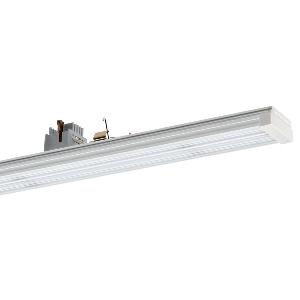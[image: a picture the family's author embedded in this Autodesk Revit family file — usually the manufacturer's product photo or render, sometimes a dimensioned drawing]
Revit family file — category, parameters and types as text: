
# Revit family: conveo_-_cvg_15000_840_xn-p_ea_5_226848239-00804961_3938
name_source: partatom
category: Lighting Fixtures
units: mm (PartAtom-declared; Revit-internal decimal feet)

## family parameters
Cut with Voids When Loaded = No
Host = Face
Light Source = No
Part Type = Normal
Room Calculation Point = No
Round Connector Dimension = Use Diameter
Shared = No

## types (1)
- CONVEO - CVG 15000/840/xN-P/EA/5 (1 x LED, 13800 lm, 4000K)
    Apparent Load = 100 VA
    Approval mark = CE
    CIE Flux Codes = 57 84 97 100 100
    Color Rendering = 80-89
    Color Temperature = 4000K
    Control Gear = Electronic ballast
    Default Elevation = 1800 mm
    Description = CVG 15000/840/xN-P/EA/5|Continuous-row system|light source: LED|work equipment: Electronic ballast|connected load: 220-240 V, 50-60 Hz|Power consumption: approx. 100 W|luminous flux: 13800 lm|luminous efficacy: 138 lm/W|colour temperature: Cold white, ca. 4000 K|color rendering index (CRI): >= 80|chromaticity tolerance:  3 SDCM|System of protection: IP 54|class of protection: I|technology: Switchable|luminaire body|material: Aluminium|surface: Powder coatet|colour: White|lamp cover: Acrylic (PMMA), Satine|weight (net): approx. 2.2 kg|Fastening: Available separately|minimum ambient temperature: -25 ░C|maximum ambient temperature: 37 ░C|glare control: Prism optics (linear)|Approval mark: VDE - ENEC|
    Frequency = 50 Hz
    Height = 70 mm
    Lamp = 1 x LED
    Lamp Light Flux = 13800 lm
    Lamp count = 1
    Length = 1500 mm
    Luminous efficacy = 138 lm/W
    Manufacturer = Waldmann
    ModVariant = No
    Model = 226848239-00804961
    Mounting Place = Ceiling
    Mounting Type = Pendant
    Number of Poles = 1
    OnlyDefault = Yes
    Power Factor = 1
    Product Name = CONVEO - CVG 15000/840/xN-P/EA/5
    Product group = Continuous-row system (industry)
    ProductGroupID = 301
    Protection Class = Protection class I
    Protection Degree = IP 54
    RLX_Detail_Level = 1
    RlxData = <blob elided: 133765 chars, md5=dc2a4953>
    Socket = socket
    Standby Power = 0 W
    System Light Flux = 13800 lm
    System Power = 100 W
    Type Comments = Product without accessories
    Type Image = 226848119-00804947-2p5.jpg
    URL = http://relux.com
    VarID = ---
    Voltage = 230 V
    Voltage Range = 220-240 V
    Weight = 0.00 kg
    Width = 64 mm

## geometry (parser evidence)
native form markers: Blend x4, Sweep x12
no freeform markers — native parametric forms only
